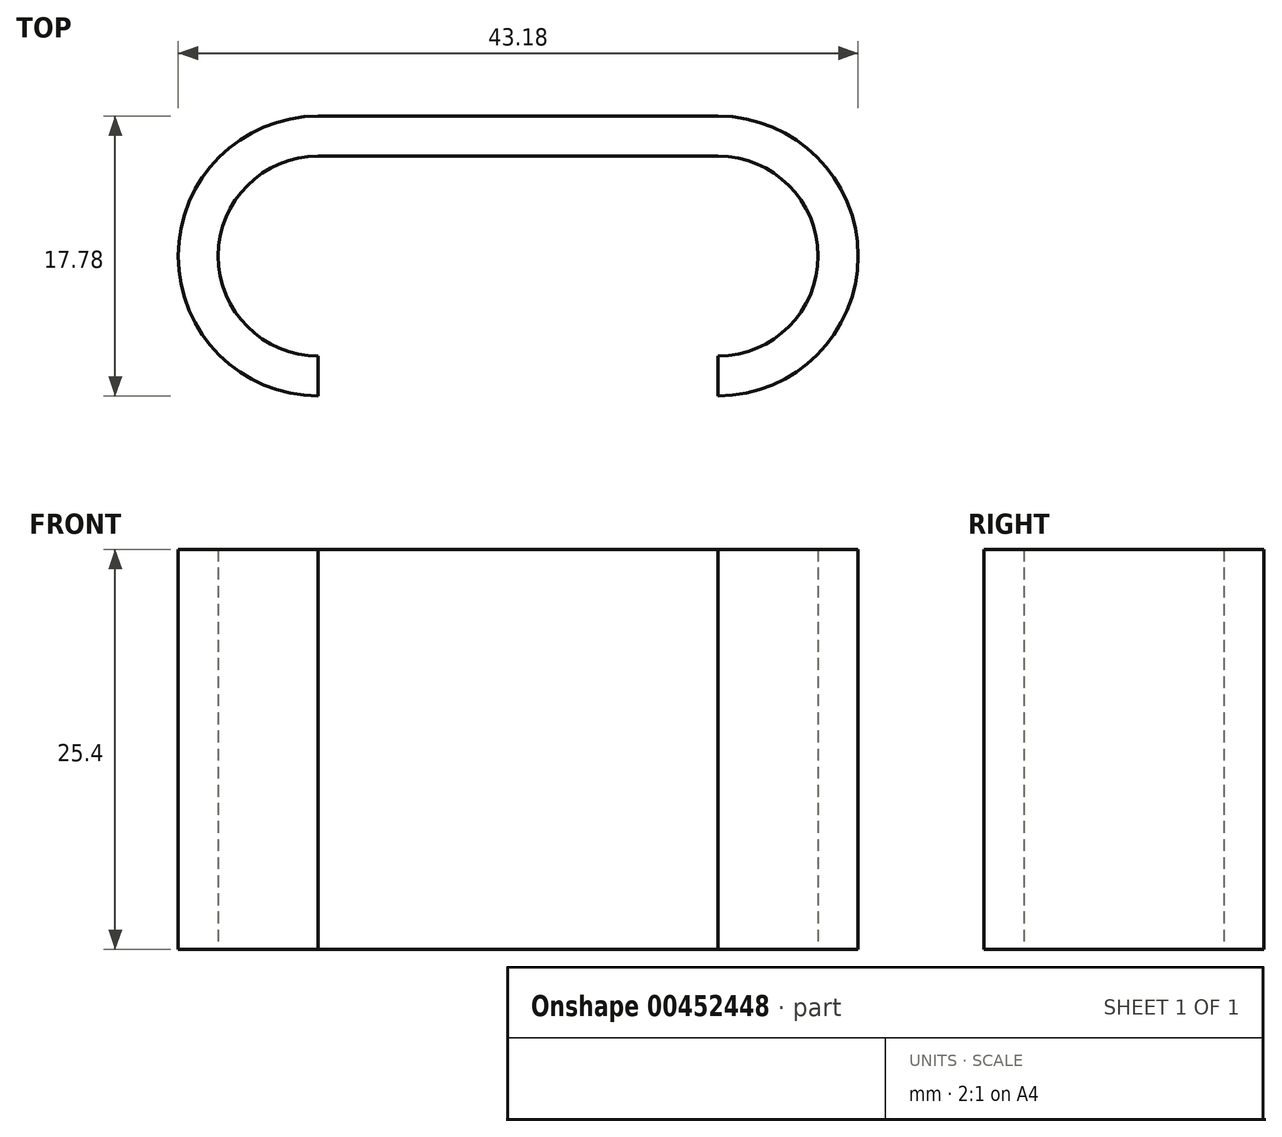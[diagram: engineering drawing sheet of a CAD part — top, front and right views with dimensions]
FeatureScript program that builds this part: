
annotation { "Feature Type Name" : "Feature", "Feature Type Description" : "" }
export const myFeature = defineFeature(function(context is Context, id is Id, definition is map)
    precondition{}
    {
        {
            var Q0;
            Q0=qCreatedBy(makeId("Top.planeOp"),FACE);
            var sketch = newSketch(context, id + "F0", { "sketchPlane" : qUnion([Q0])});
            skLineSegment(sketch, "E0.bottom", {"start": v(12.7, -6.35) * mm, "end": v(-12.7, -6.35) * mm});
            skLineSegment(sketch, "E0.top", {"start": v(12.7, 6.35) * mm, "end": v(-12.7, 6.35) * mm});
            skLineSegment(sketch, "E0.left", {"start": v(12.7, -6.35) * mm, "end": v(12.7, 6.35) * mm});
            skLineSegment(sketch, "E0.right", {"start": v(-12.7, -6.35) * mm, "end": v(-12.7, 6.35) * mm});
            skPoint(sketch, "E0.middle", {"position": v(0, 0) * mm});
            skCircle(sketch, "E1", {"center": v(12.7, 0) * mm, "radius": 6.35 * mm});
            skCircle(sketch, "E2", {"center": v(-12.7, 0) * mm, "radius": 6.35 * mm});
            skCircle(sketch, "E3", {"center": v(-12.7, 0) * mm, "radius": 8.9 * mm});
            skCircle(sketch, "E4", {"center": v(12.7, 0) * mm, "radius": 8.9 * mm});
            skLineSegment(sketch, "E5.top", {"start": v(12.7, -8.9) * mm, "end": v(-12.7, -8.9) * mm});
            skLineSegment(sketch, "E5.left", {"start": v(12.7, -6.35) * mm, "end": v(12.7, -8.9) * mm});
            skLineSegment(sketch, "E5.right", {"start": v(-12.7, -6.35) * mm, "end": v(-12.7, -8.9) * mm});
            skLineSegment(sketch, "E6.bottom", {"start": v(-12.7, 6.35) * mm, "end": v(12.7, 6.35) * mm});
            skLineSegment(sketch, "E6.top", {"start": v(-12.7, 8.89) * mm, "end": v(12.7, 8.9) * mm});
            skLineSegment(sketch, "E6.left", {"start": v(-12.7, 6.35) * mm, "end": v(-12.7, 8.89) * mm});
            skLineSegment(sketch, "E6.right", {"start": v(12.7, 6.35) * mm, "end": v(12.7, 8.9) * mm});
            skSolve(sketch);
        }
        {
            var Q0;
            {var subQ0=sQuery(id+"F0.wireOp",EDGE,"E5.right");Q0=makeQuery(id+"F0.imprint","IMPRINT",FACE,{"disambiguationData":[TD([[makeQuery(id+"F0.imprint","IMPRINT",EDGE,{"derivedFrom":subQ0}),-1.0]])]});}
            var Q1;
            {var subQ0=sQuery(id+"F0.wireOp",EDGE,"E6.top");Q1=makeQuery(id+"F0.imprint","IMPRINT",FACE,{"disambiguationData":[TD([[makeQuery(id+"F0.imprint","IMPRINT",EDGE,{"derivedFrom":subQ0}),-1.0]])]});}
            var Q2;
            {var subQ0=sQuery(id+"F0.wireOp",EDGE,"E6.right");Q2=makeQuery(id+"F0.imprint","IMPRINT",FACE,{"disambiguationData":[TD([[makeQuery(id+"F0.imprint","IMPRINT",EDGE,{"derivedFrom":subQ0}),1.0]])]});}
            var Q3;
            {var subQ0=sQuery(id+"F0.wireOp",EDGE,"E6.left");Q3=makeQuery(id+"F0.imprint","IMPRINT",FACE,{"disambiguationData":[TD([[makeQuery(id+"F0.imprint","IMPRINT",EDGE,{"derivedFrom":subQ0}),-1.0]])]});}
            var Q4;
            {var subQ0=sQuery(id+"F0.wireOp",EDGE,"E5.left");Q4=makeQuery(id+"F0.imprint","IMPRINT",FACE,{"disambiguationData":[TD([[makeQuery(id+"F0.imprint","IMPRINT",EDGE,{"derivedFrom":subQ0}),1.0]])]});}
            extrude(context, id + "F1", {"entities" : qUnion([Q0, Q1, Q2, Q3, Q4]), "depth" : 25.4 * mm});
        }
    });
